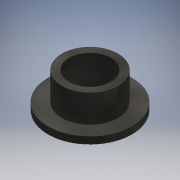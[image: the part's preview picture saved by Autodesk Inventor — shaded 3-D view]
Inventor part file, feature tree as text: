
AUTODESK INVENTOR PART (.ipt)
format: ipt  version: 2020.2 (Build 242310000, 310)  size: 108,032 bytes
history: native  units: mm
features: extrude x2, other x1, sketch x1
ambient origin geometry x8: Origin, YZ Plane, XZ Plane, XY Plane, X Axis, Y Axis, Z Axis, Center Point
bodies: Body1 (feature_tree)
feature tree (4):
  other  "ソリッド1"
  sketch  "スケッチ1"
  extrude  "押し出し1"  Depth=6.0mm
  extrude  "押し出し2"  Depth=8.0mm
